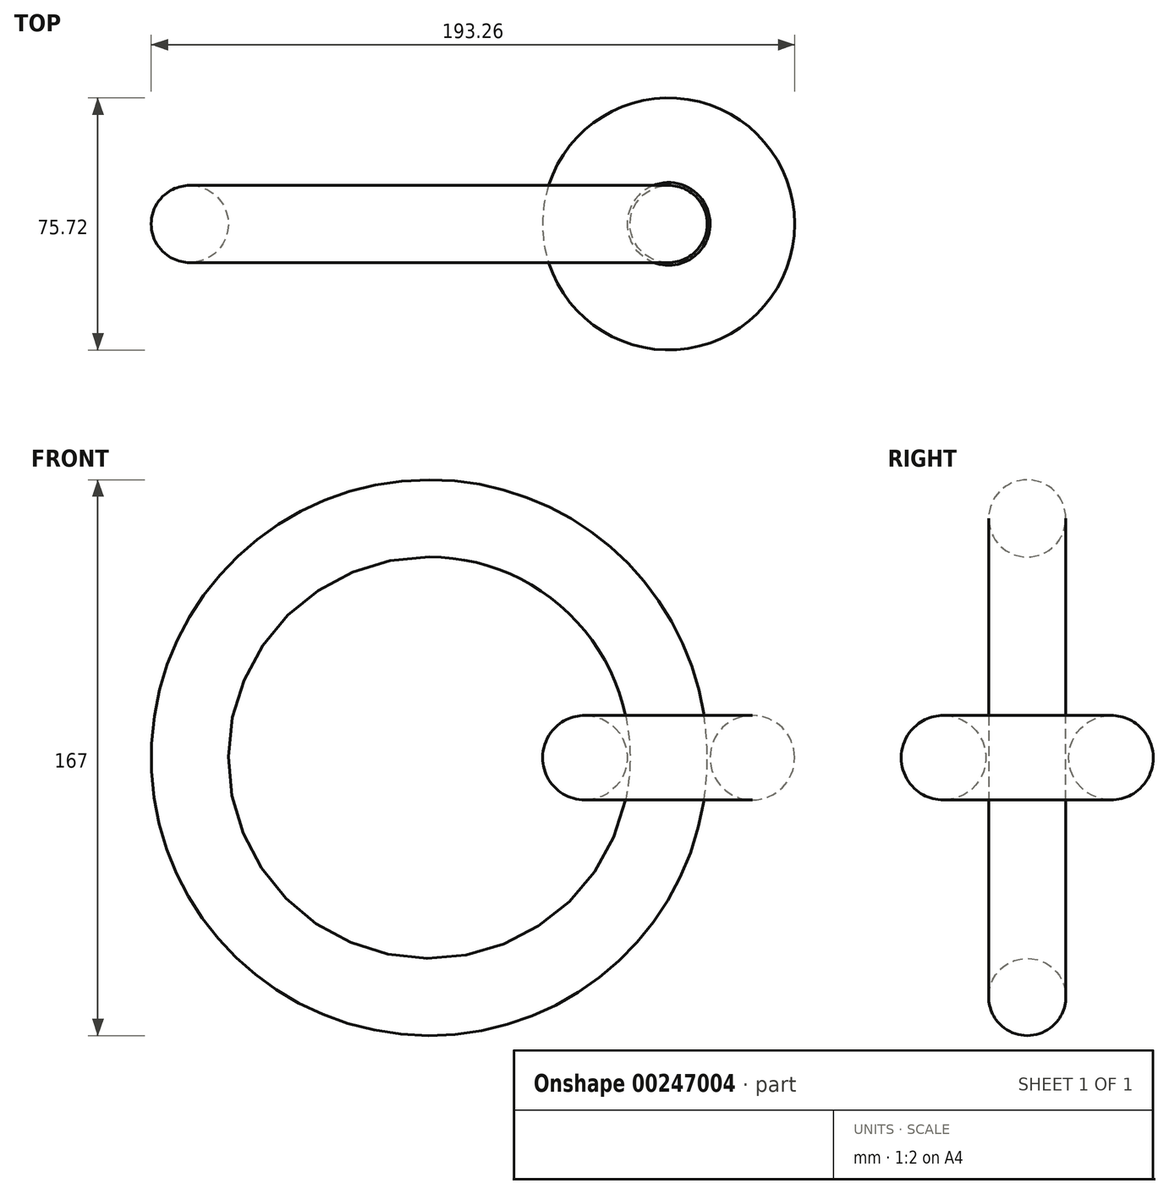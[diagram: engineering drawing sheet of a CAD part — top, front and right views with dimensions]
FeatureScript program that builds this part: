
annotation { "Feature Type Name" : "Feature", "Feature Type Description" : "" }
export const myFeature = defineFeature(function(context is Context, id is Id, definition is map)
    precondition{}
    {
        {
            var Q0;
            Q0=qCreatedBy(makeId("Front.planeOp"),FACE);
            var sketch = newSketch(context, id + "F0", { "sketchPlane" : qUnion([Q0])});
            skCircle(sketch, "E0", {"center": v(25.16, 0) * mm, "radius": 12.7 * mm});
            skSolve(sketch);
        }
        {
            var Q0;
            Q0=qCreatedBy(makeId("Front.planeOp"),FACE);
            var sketch = newSketch(context, id + "F1", { "sketchPlane" : qUnion([Q0])});
            skLineSegment(sketch, "E1", {"start": v(0, 56.41) * mm, "end": v(0, -49.19) * mm, "construction": true});
            skSolve(sketch);
        }
        {
            var Q0;
            Q0 = qSketchRegion(id + "F1", true);
            var Q1;
            Q1=makeQuery(id+"F0.imprint","IMPRINT",FACE,{"disambiguationData":[TD([[makeQuery(id+"F0.imprint","IMPRINT",EDGE,{"derivedFrom":sQuery(id+"F0.wireOp",EDGE,"E0")}),1.0]])]});
            var Q2;
            Q2=sQuery(id+"F1.wireOp",EDGE,"E1");
            revolve(context, id + "F2", {"entities" : qUnion([Q0, Q1]), "axis" : qUnion([Q2]), "revolveType" : RevolveType.FULL});
        }
        {
            var Q0;
            Q0=qCreatedBy(makeId("Top.planeOp"),FACE);
            var sketch = newSketch(context, id + "F3", { "sketchPlane" : qUnion([Q0])});
            skCircle(sketch, "E2", {"center": v(0, 0) * mm, "radius": 11.59 * mm});
            skLineSegment(sketch, "E3", {"start": v(-71.9, 26.24) * mm, "end": v(-71.9, -57.2) * mm, "construction": true});
            skSolve(sketch);
        }
        {
            var Q0;
            Q0 = qSketchRegion(id + "F3", true);
            var Q1;
            Q1=sQuery(id+"F3.wireOp",EDGE,"E3");
            revolve(context, id + "F4", {"entities" : qUnion([Q0]), "axis" : qUnion([Q1]), "revolveType" : RevolveType.FULL});
        }
    });
